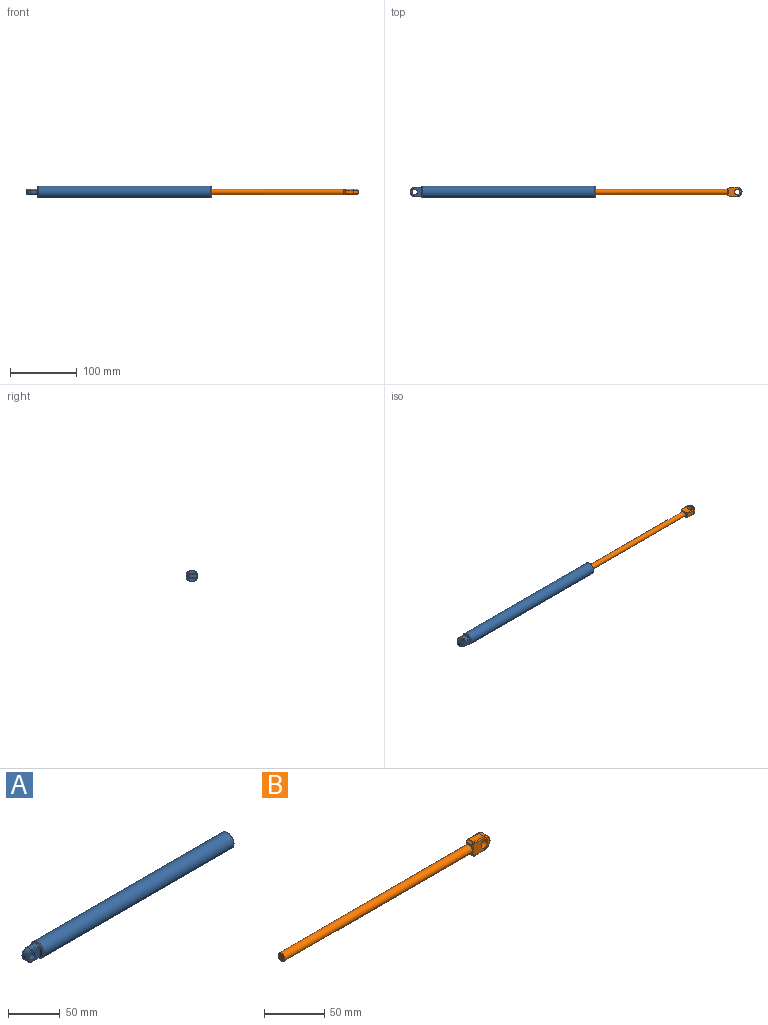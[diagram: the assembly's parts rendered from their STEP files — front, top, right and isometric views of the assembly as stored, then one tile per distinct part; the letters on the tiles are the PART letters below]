
ASSEMBLY  parts=2 mates=1
PART A: 19 faces, bbox 279.6x19.5x19.5 mm
  f0: plane 10x6mm, normal (0,0,1), area 60mm2, adj f1,f6,f11,f18
  f1: cylinder r=7.05mm len=14.1mm, axis (0,1,0), area 132.9mm2, adj f0,f2,f12,f17
  f2: plane 10x6mm, normal (0,0,-1), area 60mm2, adj f1,f6,f13,f16
  f3: cylinder r=4.05mm len=8.1mm, axis (0,1,0), area 203.6mm2, adj f4,f5
  f4: plane 16.05x12.1mm, normal (0,-1,0), area 127mm2, adj f3,f6,f11,f12,f13
  f5: plane 16.05x12.1mm, normal (0,1,0), area 127mm2, adj f3,f6,f16,f17,f18
  f6: plane 16x16mm, normal (-1,0,0), area 89.1mm2, adj f0,f2,f4,f5,f11,f13,f14,f16
  f7: cylinder r=9mm len=259.95mm, axis (1,0,0), area 14699.8mm2, adj f14,f15
  f8: plane 8.2x8.2mm, normal (1,0,0), area 52.8mm2, adj f9
  f9: cylinder r=4.1mm len=257.95mm, axis (1,0,0), area 6645.1mm2, adj f8,f10
  f10: plane 16x16mm, normal (1,0,0), area 148.3mm2, adj f9,f15
  f11: cylinder r=1mm len=10mm, axis (1,0,0), area 15.7mm2, adj f0,f4,f6,f12
  f12: torus R=6.05mm, axis (0,-1,0), area 33mm2, adj f1,f4,f11,f13
  f13: cylinder r=1mm len=10mm, axis (-1,0,0), area 15.7mm2, adj f2,f4,f6,f12
  f14: torus R=8mm, axis (-1,0,0), area 85.2mm2, adj f6,f7
  f15: torus R=8mm, axis (-1,0,0), area 85.2mm2, adj f7,f10
  f16: cylinder r=1mm len=10mm, axis (1,0,0), area 15.7mm2, adj f2,f5,f6,f17
  f17: torus R=6.05mm, axis (0,-1,0), area 33mm2, adj f1,f5,f16,f18
  f18: cylinder r=1mm len=10mm, axis (-1,0,0), area 15.7mm2, adj f0,f5,f6,f17
PART B: 42 faces, bbox 242x8.3x15.5 mm
  f0: plane 6x1.99mm, normal (-1,0,0), area 6.3mm2, adj f8,f17,f29,f30
  f1: plane 6x1.99mm, normal (-1,0,0), area 6.3mm2, adj f8,f13,f18,f19
  f2: plane 11.64x6mm, normal (0,0,-1), area 69.8mm2, adj f3,f27,f36,f41
  f3: cylinder r=7.05mm len=14.1mm, axis (0,1,0), area 132.9mm2, adj f2,f5,f22,f40
  f4: cylinder r=4.05mm len=8.1mm, axis (0,1,0), area 203.6mm2, adj f6,f7
  f5: plane 11.64x6mm, normal (0,0,1), area 69.8mm2, adj f3,f21,f32,f38
  f6: plane 20.38x12.38mm, normal (0,-1,0), area 163.8mm2, adj f4,f15,f18,f24,f30,f31,f37,f38
  f7: plane 20.38x12.38mm, normal (0,1,0), area 163.8mm2, adj f4,f12,f13,f14,f17,f20,f21,f22
  f8: cylinder r=4mm len=220mm, axis (-1,0,0), area 5529.2mm2, adj f0,f1,f9,f12,f14,f15,f24
  f9: plane 8x8mm, normal (-1,0,0), area 50.3mm2, adj f8
  f10: plane 6x1.41mm, normal (-0.71,0,-0.71), area 12mm2, adj f28,f29,f36,f37
  f11: plane 6x1.41mm, normal (-0.71,0,0.71), area 12mm2, adj f19,f20,f31,f32
  f12: bspline ~2.99x1.18mm, area 1.3mm2, adj f7,f8,f13
  f13: cylinder r=1mm len=1.99mm, axis (0,0,-1), area 3.1mm2, adj f1,f7,f12,f16
  f14: bspline ~2.99x1.18mm, area 1.3mm2, adj f7,f8,f17
  f15: bspline ~2.99x1.18mm, area 1.3mm2, adj f6,f8,f18
  f16: sphere r=1mm, area 0.6mm2, adj f13,f19,f20
  f17: cylinder r=1mm len=1.99mm, axis (0,0,-1), area 3.1mm2, adj f0,f7,f14,f23
  f18: cylinder r=1mm len=1.99mm, axis (0,0,1), area 3.1mm2, adj f1,f6,f15,f25
  f19: cylinder r=1mm len=6mm, axis (0,-1,0), area 4.7mm2, adj f1,f11,f16,f25
  f20: cylinder r=1mm len=2.12mm, axis (-0.71,0,-0.71), area 3.1mm2, adj f7,f11,f16,f26
  f21: cylinder r=1mm len=11.64mm, axis (-1,0,0), area 18.3mm2, adj f5,f7,f22,f26
  f22: torus R=6.05mm, axis (0,-1,0), area 33mm2, adj f3,f7,f21,f27
  f23: sphere r=1mm, area 0.6mm2, adj f17,f28,f29
  f24: bspline ~2.99x1.18mm, area 1.3mm2, adj f6,f8,f30
  f25: sphere r=1mm, area 0.6mm2, adj f18,f19,f31
  f26: sphere r=1mm, area 1mm2, adj f20,f21,f32
  f27: cylinder r=1mm len=11.64mm, axis (1,0,0), area 18.3mm2, adj f2,f7,f22,f33
  f28: cylinder r=1mm len=2.12mm, axis (-0.71,0,0.71), area 3.1mm2, adj f7,f10,f23,f33
  f29: cylinder r=1mm len=6mm, axis (0,-1,0), area 4.7mm2, adj f0,f10,f23,f34
  f30: cylinder r=1mm len=1.99mm, axis (0,0,1), area 3.1mm2, adj f0,f6,f24,f34
  f31: cylinder r=1mm len=2.12mm, axis (-0.71,0,-0.71), area 3.1mm2, adj f6,f11,f25,f35
  f32: cylinder r=1mm len=6mm, axis (0,-1,0), area 4.7mm2, adj f5,f11,f26,f35
  f33: sphere r=1mm, area 1mm2, adj f27,f28,f36
  f34: sphere r=1mm, area 0.6mm2, adj f29,f30,f37
  f35: sphere r=1mm, area 1mm2, adj f31,f32,f38
  f36: cylinder r=1mm len=6mm, axis (0,1,0), area 4.7mm2, adj f2,f10,f33,f39
  f37: cylinder r=1mm len=2.12mm, axis (-0.71,0,0.71), area 3.1mm2, adj f6,f10,f34,f39
  f38: cylinder r=1mm len=11.64mm, axis (1,0,0), area 18.3mm2, adj f5,f6,f35,f40
  f39: sphere r=1mm, area 1mm2, adj f36,f37,f41
  f40: torus R=6.05mm, axis (0,-1,0), area 33mm2, adj f3,f6,f38,f41
  f41: cylinder r=1mm len=11.64mm, axis (-1,0,0), area 18.3mm2, adj f2,f6,f39,f40
PLACE A rot(axis=(1,0,0),90deg) t=(486,0,0)mm
PLACE B rot(axis=(1,0,0),90deg) t=(485,0,0)mm
MATE slider A.f15 <-> B.f8  axis (1,0,0) through (270.95,0,0)mm
